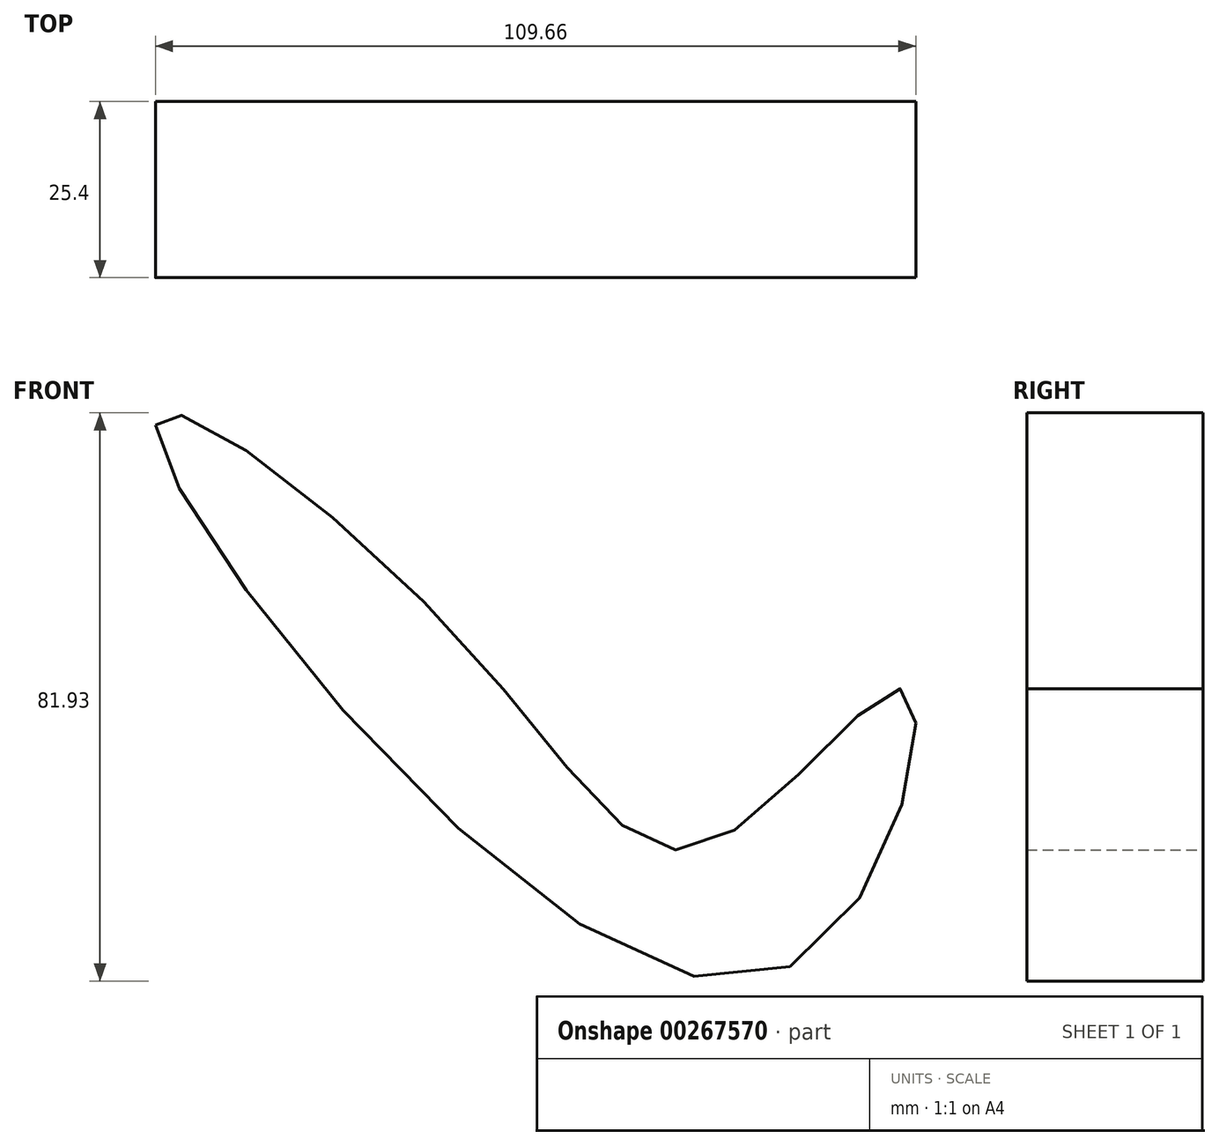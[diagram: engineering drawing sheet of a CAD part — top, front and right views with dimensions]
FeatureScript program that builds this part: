
annotation { "Feature Type Name" : "Feature", "Feature Type Description" : "" }
export const myFeature = defineFeature(function(context is Context, id is Id, definition is map)
    precondition{}
    {
        {
            var Q0;
            Q0=qCreatedBy(makeId("Front.planeOp"),FACE);
            var sketch = newSketch(context, id + "F0", { "sketchPlane" : qUnion([Q0])});
            skFitSpline(sketch, "E0", {"points": [v(-66.73, 14.45) * mm, v(19.5, -65.44) * mm, v(41.6, -23.85) * mm, v(13.16, -45.94) * mm, v(-21.85, -17.5) * mm, v(-66.73, 14.45) * mm]});
            skSolve(sketch);
        }
        {
            var Q0;
            Q0 = qSketchRegion(id + "F0", true);
            extrude(context, id + "F1", {"entities" : qUnion([Q0]), "depth" : 25.4 * mm});
        }
    });
